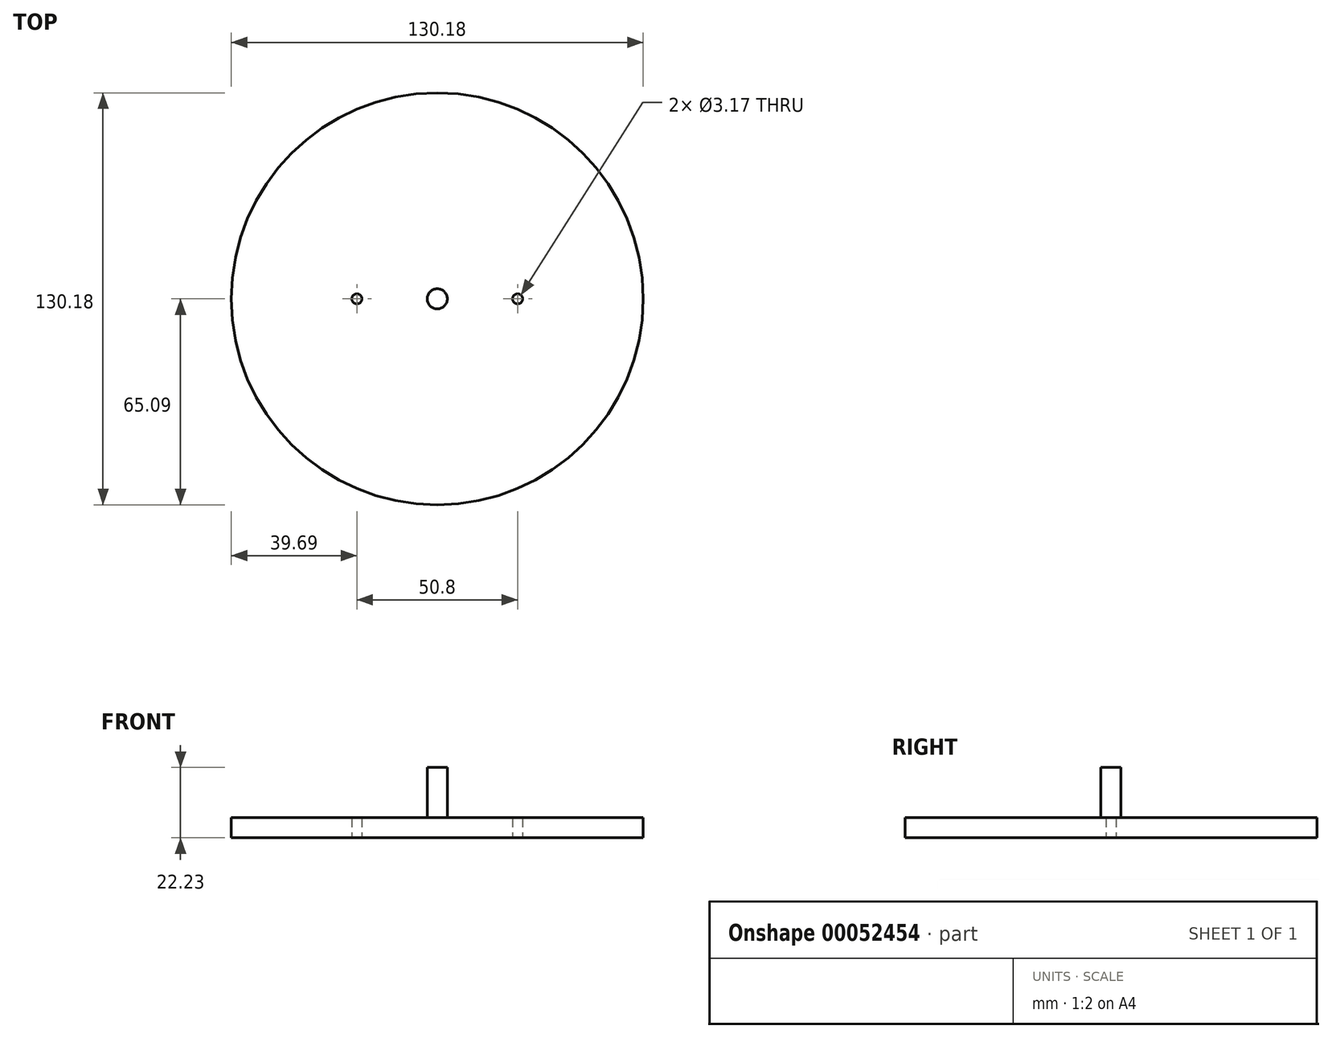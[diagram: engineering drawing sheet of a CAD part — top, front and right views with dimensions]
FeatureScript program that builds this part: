
annotation { "Feature Type Name" : "Feature", "Feature Type Description" : "" }
export const myFeature = defineFeature(function(context is Context, id is Id, definition is map)
    precondition{}
    {
        {
            var Q0;
            Q0=qCreatedBy(makeId("Top.planeOp"),FACE);
            var sketch = newSketch(context, id + "F0", { "sketchPlane" : qUnion([Q0])});
            skCircle(sketch, "E0", {"center": v(0, 0) * mm, "radius": 65.09 * mm});
            skLineSegment(sketch, "E1", {"start": v(0, 65.09) * mm, "end": v(0, -65.09) * mm});
            skLineSegment(sketch, "E2", {"start": v(-65.09, 0) * mm, "end": v(65.09, 0) * mm});
            skLineSegment(sketch, "E3", {"start": v(0, 0) * mm, "end": v(-25.4, 0) * mm});
            skLineSegment(sketch, "E4", {"start": v(0, 0) * mm, "end": v(25.4, 0) * mm});
            skCircle(sketch, "E5", {"center": v(-25.4, 0) * mm, "radius": 1.59 * mm});
            skCircle(sketch, "E6", {"center": v(25.4, 0) * mm, "radius": 1.59 * mm});
            skCircle(sketch, "E7", {"center": v(0, 0) * mm, "radius": 3.18 * mm});
            skSolve(sketch);
        }
        {
            var Q0;
            {var subQ1=sQuery(id+"F0.wireOp",EDGE,"E1");var subQ3=sQuery(id+"F0.wireOp",EDGE,"E7");var subQ4=makeQuery(id+"F0.imprint","INTERSECT",VERTEX,{"disambiguationData":[OD(0.0)],"derivedFrom":[subQ1,subQ3]});Q0=makeQuery(id+"F0.imprint","IMPRINT",FACE,{"disambiguationData":[TD([[makeQuery(id+"F0.imprint","IMPRINT",EDGE,{"disambiguationData":[TD([[subQ4,1.0]])],"derivedFrom":subQ3}),1.0]])]});}
            var Q1;
            {var subQ1=sQuery(id+"F0.wireOp",EDGE,"E1");var subQ3=sQuery(id+"F0.wireOp",EDGE,"E7");var subQ4=makeQuery(id+"F0.imprint","INTERSECT",VERTEX,{"disambiguationData":[OD(0.0)],"derivedFrom":[subQ1,subQ3]});Q1=makeQuery(id+"F0.imprint","IMPRINT",FACE,{"disambiguationData":[TD([[makeQuery(id+"F0.imprint","IMPRINT",EDGE,{"disambiguationData":[TD([[subQ4,-1.0]])],"derivedFrom":subQ3}),1.0]])]});}
            var Q2;
            {var subQ1=sQuery(id+"F0.wireOp",EDGE,"E1");var subQ3=sQuery(id+"F0.wireOp",EDGE,"E7");var subQ4=makeQuery(id+"F0.imprint","INTERSECT",VERTEX,{"disambiguationData":[OD(1.0)],"derivedFrom":[subQ1,subQ3]});Q2=makeQuery(id+"F0.imprint","IMPRINT",FACE,{"disambiguationData":[TD([[makeQuery(id+"F0.imprint","IMPRINT",EDGE,{"disambiguationData":[TD([[subQ4,1.0]])],"derivedFrom":subQ3}),1.0]])]});}
            var Q3;
            {var subQ1=sQuery(id+"F0.wireOp",EDGE,"E1");var subQ3=sQuery(id+"F0.wireOp",EDGE,"E7");var subQ4=makeQuery(id+"F0.imprint","INTERSECT",VERTEX,{"disambiguationData":[OD(1.0)],"derivedFrom":[subQ1,subQ3]});Q3=makeQuery(id+"F0.imprint","IMPRINT",FACE,{"disambiguationData":[TD([[makeQuery(id+"F0.imprint","IMPRINT",EDGE,{"disambiguationData":[TD([[subQ4,-1.0]])],"derivedFrom":subQ3}),1.0]])]});}
            extrude(context, id + "F1", {"entities" : qUnion([Q0, Q1, Q2, Q3]), "depth" : 19.05 * mm});
        }
        {
            var Q0;
            Q0 = qSketchRegion(id + "F0", true);
            extrude(context, id + "F2", {"entities" : qUnion([Q0]), "operationType" : NewBodyOperationType.ADD, "depth" : 3.17 * mm});
        }
        {
            var Q0;
            {var subQ0=sQuery(id+"F0.wireOp",EDGE,"E7");Q0=makeQuery(id+"F2.boolean.opBoolean","MERGE",FACE,{"derivedFrom":[makeQuery(id+"F1.opExtrude","CAP_FACE",FACE,{"disambiguationData":[OSD([subQ0])],"isStart":true}),makeQuery(id+"F2.opExtrude","CAP_FACE",FACE,{"disambiguationData":[OSD([sQuery(id+"F0.wireOp",EDGE,"E0"),sQuery(id+"F0.wireOp",EDGE,"E5"),sQuery(id+"F0.wireOp",EDGE,"E6"),subQ0])],"isStart":true})]});}
            extrude(context, id + "F3", {"entities" : qUnion([Q0]), "operationType" : NewBodyOperationType.ADD, "depth" : 3.17 * mm});
        }
    });
